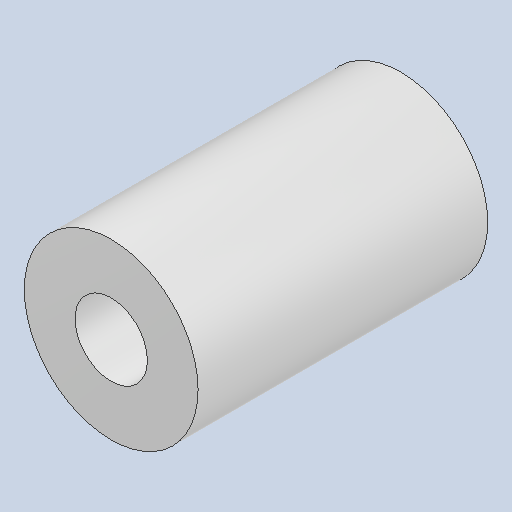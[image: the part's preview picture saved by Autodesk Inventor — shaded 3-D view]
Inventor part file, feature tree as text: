
AUTODESK INVENTOR PART (.ipt)
format: ipt  version: 2023 (Build 270158000, 158)  size: 206,848 bytes
history: native  units: mm
features: extrude x1, sketch x1
ambient origin geometry x8: Origin, YZ Plane, XZ Plane, XY Plane, X Axis, Y Axis, Z Axis, Center Point
bodies: Solid1 (feature_tree)
feature tree (2):
  extrude  "Extrusion1"  Depth=10.0mm
  sketch  "Sketch1"  dims[d0=2.5mm d1=6.0mm d2=10.0mm d3=0.0mm]
